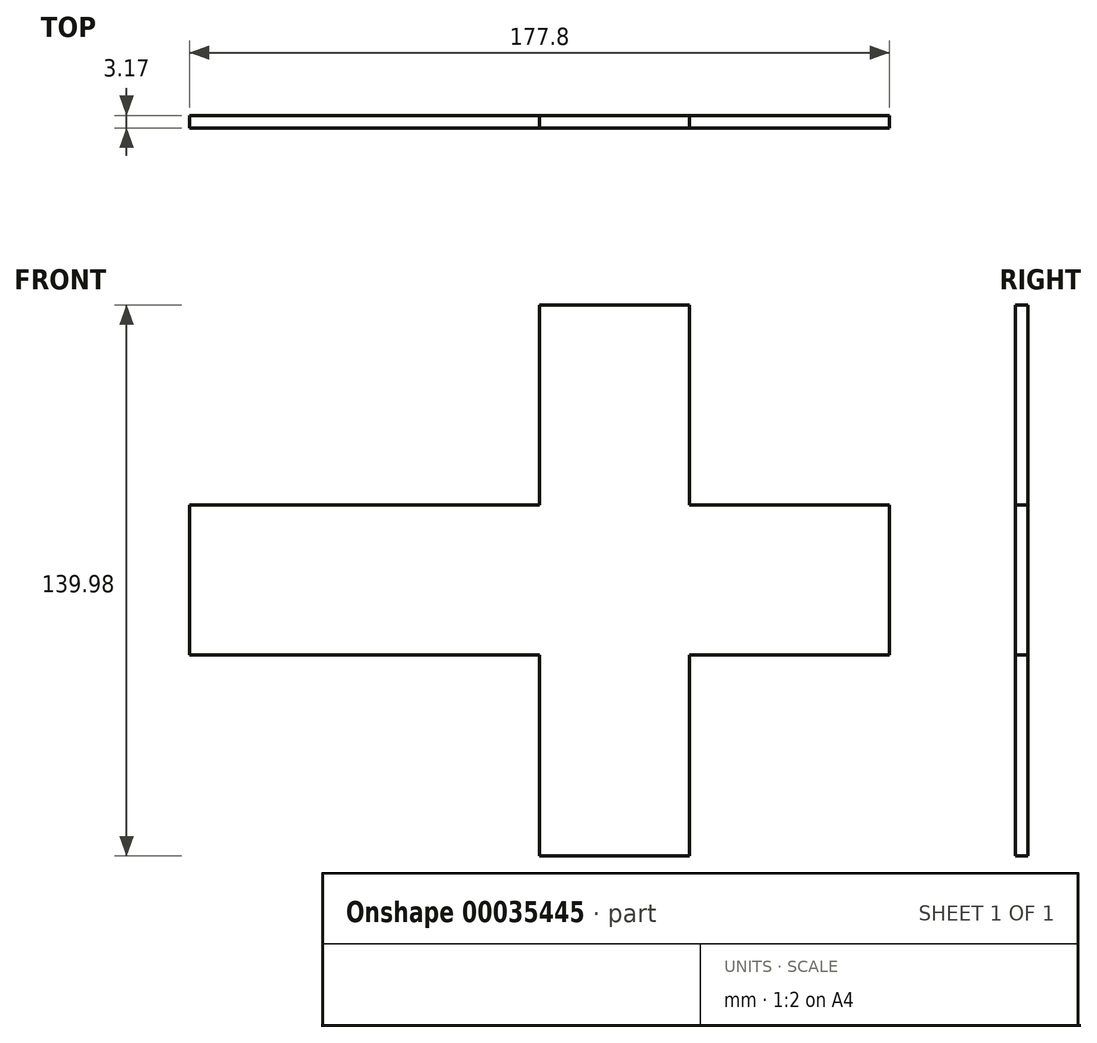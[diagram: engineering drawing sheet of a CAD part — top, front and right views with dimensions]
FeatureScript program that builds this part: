
annotation { "Feature Type Name" : "Feature", "Feature Type Description" : "" }
export const myFeature = defineFeature(function(context is Context, id is Id, definition is map)
    precondition{}
    {
        {
            var Q0;
            Q0=qCreatedBy(makeId("Front.planeOp"),FACE);
            var sketch = newSketch(context, id + "F0", { "sketchPlane" : qUnion([Q0])});
            skLineSegment(sketch, "E0.bottom", {"start": v(-15.44, 21.58) * mm, "end": v(22.66, 21.58) * mm});
            skLineSegment(sketch, "E0.top", {"start": v(-15.44, -16.8) * mm, "end": v(22.66, -16.8) * mm});
            skLineSegment(sketch, "E0.left", {"start": v(-15.44, 21.58) * mm, "end": v(-15.44, -16.8) * mm});
            skLineSegment(sketch, "E0.right", {"start": v(22.66, 21.58) * mm, "end": v(22.66, -16.8) * mm});
            skLineSegment(sketch, "E1.bottom", {"start": v(22.66, -16.8) * mm, "end": v(-15.44, -16.8) * mm});
            skLineSegment(sketch, "E1.top", {"start": v(22.66, -67.6) * mm, "end": v(-15.44, -67.6) * mm});
            skLineSegment(sketch, "E1.left", {"start": v(22.66, -16.8) * mm, "end": v(22.66, -67.6) * mm});
            skLineSegment(sketch, "E1.right", {"start": v(-15.44, -16.8) * mm, "end": v(-15.44, -67.6) * mm});
            skLineSegment(sketch, "E2.top", {"start": v(-15.44, 72.38) * mm, "end": v(22.66, 72.38) * mm});
            skLineSegment(sketch, "E2.left", {"start": v(-15.44, 21.58) * mm, "end": v(-15.44, 72.38) * mm});
            skLineSegment(sketch, "E2.right", {"start": v(22.66, 21.58) * mm, "end": v(22.66, 72.38) * mm});
            skLineSegment(sketch, "E3.bottom", {"start": v(22.66, 21.58) * mm, "end": v(73.46, 21.58) * mm});
            skLineSegment(sketch, "E3.top", {"start": v(22.66, -16.52) * mm, "end": v(73.46, -16.52) * mm});
            skLineSegment(sketch, "E3.left", {"start": v(22.66, 21.58) * mm, "end": v(22.66, -16.52) * mm});
            skLineSegment(sketch, "E3.right", {"start": v(73.46, 21.58) * mm, "end": v(73.46, -16.52) * mm});
            skLineSegment(sketch, "E4.bottom", {"start": v(-15.44, 21.58) * mm, "end": v(-66.24, 21.58) * mm});
            skLineSegment(sketch, "E4.top", {"start": v(-15.44, -16.52) * mm, "end": v(-66.24, -16.52) * mm});
            skLineSegment(sketch, "E4.left", {"start": v(-15.44, 21.58) * mm, "end": v(-15.44, -16.52) * mm});
            skLineSegment(sketch, "E4.right", {"start": v(-66.24, 21.58) * mm, "end": v(-66.24, -16.52) * mm});
            skLineSegment(sketch, "E5.bottom", {"start": v(-66.24, 21.58) * mm, "end": v(-104.34, 21.58) * mm});
            skLineSegment(sketch, "E5.top", {"start": v(-66.24, -16.52) * mm, "end": v(-104.34, -16.52) * mm});
            skLineSegment(sketch, "E5.right", {"start": v(-104.34, 21.58) * mm, "end": v(-104.34, -16.52) * mm});
            skSolve(sketch);
        }
        {
            var Q0;
            Q0 = qSketchRegion(id + "F0", true);
            extrude(context, id + "F1", {"entities" : qUnion([Q0]), "oppositeDirection" : true, "depth" : 3.17 * mm});
        }
    });
